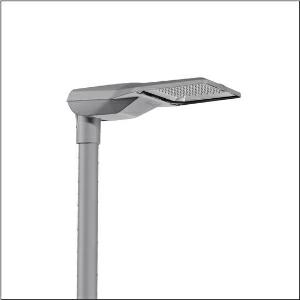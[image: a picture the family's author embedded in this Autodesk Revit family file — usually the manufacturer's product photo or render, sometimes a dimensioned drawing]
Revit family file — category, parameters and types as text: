
# Revit family: streetlight_sl_21_midi___pc-r_5xe7g43a08mb_b1b0
name_source: partatom
category: Lighting Fixtures
units: mm (PartAtom-declared; Revit-internal decimal feet)

## family parameters
Cut with Voids When Loaded = No
Host = Face
Light Source = No
Part Type = Normal
Room Calculation Point = No
Round Connector Dimension = Use Diameter
Shared = No

## types (1)
- --- (1 x LED, 19200 lm, 147 W, 4000K)
    Apparent Load = 147 VA
    CIE Flux Codes = 38 78 98 100 100
    Color Rendering = 70
    Color Temperature = 4000K
    Default Elevation = 1800 mm
    Description = Streetlight SL 21 midi, mast luminaire, primary light control with lens, of PMMA, primary optical cover: cover, of toughened safety glass, transparent, light distribution: PC-R, light emission: direct distribution, primary light characteristic: asymmetric, right, installation type: post-top, side-entry, LED, 3G 1.5mm², High Power LED, rated luminous flux: 19.200lm, luminous efficacy: 131lm/W, light colour: 740, colour temperature: 4000K, control: overheat protection, constant luminous flux control, time-dependent luminous flux control, flexible luminous flux parameterisation, mains connection: 220..240V, AC, 50/60Hz, connection cable pre-assembled, cable length: 12,5m, wiring characteristics: H07RN-F, start of lifetime: 147W, end of service life: 155W, reduction: 64W, luminaire housing, of diecast aluminium, powder-coated, Siteco® metallic grey (DB 702S), corrosivity category C5 mid according to DIN EN ISO 12944, please order mast flange separately, inclination adjustable: 0°, 5°, 10°, 15°, sealing non-destructively replaceable, multi-level sealing system, length: 644mm, width: 335mm, height: 110mm, mast flange for spigot size: 42mm (side-entry): 5XC10008XM4, 60/48mm (side-entry/post-top): 5XC10108XM2, 76/60mm (side-entry/post-top): 5XC10108XM1, protection rating (complete): IP66, insulation class (complete): insulation class II (safety insulation), certification: CE, ENEC, ENEC+, VDE, impact resistance: IK09, permissible operating ambient temperature for outdoor applications: -40..+50°C, standard-compliant lighting for roads and squares, packaging unit: 1 piece

Light Distribution: PC-R
    Height = 111 mm
    Lamp = 1 x LED
    Lamp Light Flux = 19200 lm
    Lamp Power = 147 W
    Lamp count = 1
    Length = 644 mm
    Luminous efficacy = 131 lm/W
    Manufacturer = Siteco
    ModVariant = No
    Model = 5XE7G43A08MB
    Number of Poles = 1
    OnlyDefault = Yes
    Power Factor = 1
    Product Name = Streetlight SL 21 midi | PC-R
    Product group = mast luminaire | pylon top
    ProductGroupID = 6100
    Protection Class = Protection class II
    Protection Degree = IP 66
    RLX_Detail_Level = 1
    RLX_Emergency_Light_Flux = 0 lm
    RLX_Emergency_Type = 0
    RLX_Emergency_Type_DB = No
    RlxData = <blob elided: 92969 chars, md5=8abb2c13>
    Socket = socket
    Standby Power = 0 W
    System Light Flux = 19200 lm
    System Power = 147 W
    Type Comments = factory setting: luminous flux: 100 % | Output Level: 100 % | 750 mA
    Type Image = l_1004298.jpg
    URL = http://relux.com
    VarID = @adj_004991
    Voltage = 0 V
    Weight = 0.00 kg
    Width = 336 mm

## geometry (parser evidence)
native form markers: Blend x4, Sweep x13
no freeform markers — native parametric forms only
